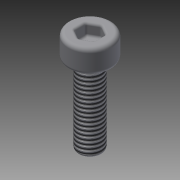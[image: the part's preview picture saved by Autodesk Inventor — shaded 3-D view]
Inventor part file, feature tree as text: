
AUTODESK INVENTOR PART (.ipt)
format: ipt  version: 2013 (Build 170138000, 138)  size: 161,792 bytes
history: native  units: mm
features: extrude x3, sketch x3, fillet x2, other x1, thread x1
ambient origin geometry x1: Origin
feature tree (10):
  other  "ソリッド1"
  extrude  "押し出し1"  Depth=5.5mm
  extrude  "押し出し2"  Depth=3.0mm TaperAngle=0.0deg
  extrude  "押し出し3"  Depth=3.0mm
  fillet  "フィレット1"  Radius=10.0mm
  fillet  "フィレット2"  Radius=1.25mm
  thread  "ねじ2"
  sketch  "スケッチ1"
  sketch  "スケッチ2"
  sketch  "スケッチ3"
